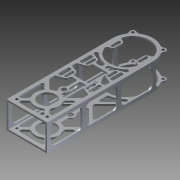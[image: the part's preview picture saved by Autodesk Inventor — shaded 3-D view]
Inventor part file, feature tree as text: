
AUTODESK INVENTOR PART (.ipt)
format: ipt  version: 2012 (Build 160160000, 160)  size: 832,000 bytes
history: native  units: in
note: dims shown in document units (in); Inventor stores cm internally (conversion verified against a paired STEP export)
features: extrude x7, sketch x5, thread x4, fillet x3
ambient origin geometry x8: Origin, YZ Plane, XZ Plane, XY Plane, X Axis, Y Axis, Z Axis, Center Point
bodies: Solid1 (feature_tree)
feature tree (19):
  extrude  "Extrusion1"  Depth=3.0in
  sketch  "Sketch2"  dims[d2=0.125in d3=0.125in d4=0.125in]
  extrude  "Extrusion2"  Depth=0.125in
  fillet  "Fillet1"  Radius=0.125in
  sketch  "Sketch3"  dims[d5=0.125in d6=10.0in d7=0.0in]
  extrude  "Extrusion3"  Depth=10.0in TaperAngle=0.0deg
  extrude  "Extrusion4"  Depth=1.5in
  fillet  "Fillet2"  Radius=1.5in
  extrude  "Extrusion5"  Depth=1.5in
  fillet  "Fillet3"  Radius=0.5in
  extrude  "Extrusion6"  Depth=0.366in
  extrude  "Extrusion7"  Depth=1.75in
  thread  "Thread1"  [1 undecoded]
  thread  "Thread2"  [1 undecoded]
  thread  "Thread3"  [1 undecoded]
  thread  "Thread4"  [1 undecoded]
  sketch  "Sketch1"  dims[d0=2.0in d1=3.0in]
  sketch  "Sketch4"  dims[d8=1.25in d9=1.5in d10=1.5in]
  sketch  "Sketch5"  dims[d11=1.3125in d15=1.5in d18=0.5in d30=0.366in d31=1.75in d32=0.125in d33=0.125in d34=0.125in d35=0.125in d36=0.125in d37=0.125in d38=0.25in d39=0.25in d41=0.25in d42=0.875in d43=1.5in d44=0.125in d45=0.125in d46=0.125in d47=0.125in d48=0.3125in d49=0.25in d50=0.0in d51=0.125in d52=0.5in d53=0.1in d54=0.5in d55=0.1in d56=0.5in d57=0.1in d58=0.5in d59=0.1in d60=1.6in d61=1.6in d62=0.5in d63=0.5in d64=0.8in d65=0.8in d66=3.0in d70=0.1in d71=2.0in d74=2.0in d75=2.5in d76=0.2in d77=0.2in d78=1.5in d79=0.25in d80=0.25in d81=0.25in d82=0.25in d83=0.1in d84=1.0in d85=0.0in d86=0.5in d87=0.5in d89=1.0in d90=7.375in d91=2.5in d92=0.366in d94=0.125in d95=0.125in d96=0.875in d97=0.25in d98=0.25in d99=0.25in d100=0.125in d101=0.125in d102=0.25in d103=0.2in d106=0.1875in d107=0.0938in d108=0.1875in d109=0.0938in d110=0.0938in d111=0.1875in d112=0.3in d113=0.125in d114=0.481in d115=0.481in d116=0.2in d119=1.4375in d120=0.1875in d121=0.0938in d123=1.2in d124=0.481in d125=0.481in d126=0.125in d127=0.0in d128=0.125in d129=0.25in d133=0.125in d172=0.125in d173=0.0in d174=0.25in d175=0.25in d176=0.25in d177=0.25in d178=0.25in d179=3.0in d181=0.125in d183=0.125in d184=2.625in d185=1.1811in d187=2.625in d188=0.3937in d190=1.0in d192=0.125in d193=0.125in d194=0.125in d195=0.125in d196=0.125in d197=0.125in d198=0.125in d199=0.125in d200=0.481in d201=1.25in d202=4.75in d203=45.0deg d204=0.0938in d205=0.1875in d206=0.1875in d209=0.0625in d210=0.0in d211=0.375in d212=0.201in d213=9.0in d214=0.375in d216=0.25in d218=0.375in d221=0.25in d222=0.625in d223=0.125in d224=0.125in d226=0.25in d227=0.0625in d228=0.0in d229=1.0in d230=0.0in d231=1.0in d232=0.0in d233=1.0in d234=0.0in d235=1.0in d236=0.0in d237=7.375in d238=0.2in]
note: 4 required parameter values undecoded (feature->parameter linkage not recoverable at this tier; creation-order binding heuristic only, values carry confidence <= 0.55)
